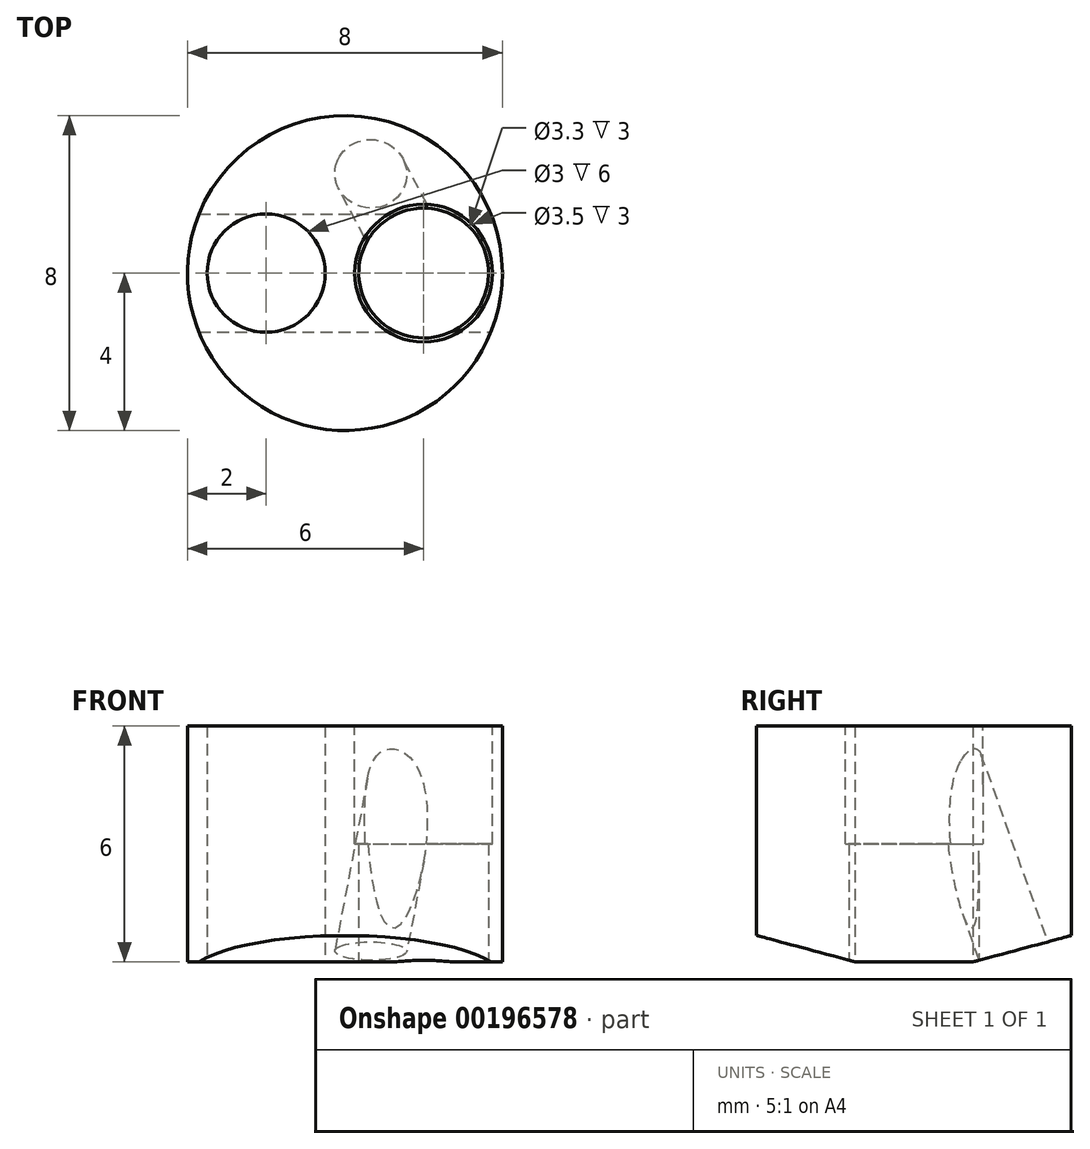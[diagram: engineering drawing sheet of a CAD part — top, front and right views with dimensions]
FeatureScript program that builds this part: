
annotation { "Feature Type Name" : "Feature", "Feature Type Description" : "" }
export const myFeature = defineFeature(function(context is Context, id is Id, definition is map)
    precondition{}
    {
        {
            var Q0;
            Q0=qCreatedBy(makeId("Top.planeOp"),FACE);
            var sketch = newSketch(context, id + "F0", { "sketchPlane" : qUnion([Q0])});
            skCircle(sketch, "E0", {"center": v(0, 0) * mm, "radius": 4 * mm});
            skCircle(sketch, "E1", {"center": v(-2, 0) * mm, "radius": 1.5 * mm});
            skPoint(sketch, "E2", {"position": v(2, 0) * mm});
            skLineSegment(sketch, "E3", {"start": v(0, -7.13) * mm, "end": v(0, 13.24) * mm, "construction": true});
            skSolve(sketch);
        }
        {
            var Q0;
            Q0 = qSketchRegion(id + "F0", true);
            extrude(context, id + "F1", {"entities" : qUnion([Q0]), "depth" : 6 * mm});
        }
        {
            var Q0;
            Q0=sQuery(id+"F0.wireOp",VERTEX,"E2");
            var Q1;
            Q1=makeQuery(id+"F1.opExtrude","SWEPT_BODY",BODY,{"disambiguationData":[OSD([sQuery(id+"F0.wireOp",EDGE,"E0"),sQuery(id+"F0.wireOp",EDGE,"E1")])]});
            hole(context, id + "F2", {"style" : HoleStyle.SIMPLE, "endStyle" : HoleEndStyle.BLIND, "oppositeDirection" : true, "standardTappedOrClearance" : lookupTablePath({ "standard" : "ISO", "fit" : "Normal", "size" : "M3", "type" : "Clearance" }), "standardBlindInLast" : lookupTablePath({ "fit" : "Standard", "standard" : "ISO", "size" : "M3", "type" : "Clearance" }), "holeDiameter" : 3.3 * mm, "holeDepth" : 3 * mm, "locations" : qUnion([Q0]), "scope" : qUnion([Q1])});
        }
        {
            var Q0;
            Q0=qCreatedBy(makeId("Right.planeOp"),FACE);
            var sketch = newSketch(context, id + "F3", { "sketchPlane" : qUnion([Q0])});
            skLineSegment(sketch, "E4", {"start": v(1.5, 0) * mm, "end": v(6.98, 1.47) * mm});
            skLineSegment(sketch, "E5", {"start": v(6.98, 1.47) * mm, "end": v(6.98, 0) * mm});
            skLineSegment(sketch, "E6", {"start": v(6.98, 0) * mm, "end": v(1.5, 0) * mm});
            skLineSegment(sketch, "E7", {"start": v(0, 0) * mm, "end": v(0, 8.53) * mm, "construction": true});
            skLineSegment(sketch, "E8.MirrorCS", {"start": v(-6.98, 1.47) * mm, "end": v(-6.98, 0) * mm});
            skLineSegment(sketch, "E9.MirrorCS", {"start": v(-6.98, 0) * mm, "end": v(-1.5, 0) * mm});
            skLineSegment(sketch, "E10.MirrorCS", {"start": v(-1.5, 0) * mm, "end": v(-6.98, 1.47) * mm});
            skSolve(sketch);
        }
        {
            var Q0;
            Q0 = qSketchRegion(id + "F3", true);
            var Q1;
            Q1=makeQuery(id+"F1.opExtrude","SWEPT_BODY",BODY,{"disambiguationData":[OSD([sQuery(id+"F0.wireOp",EDGE,"E0"),sQuery(id+"F0.wireOp",EDGE,"E1")])]});
            extrude(context, id + "F4", {"entities" : qUnion([Q0]), "operationType" : NewBodyOperationType.REMOVE, "endBound" : BoundingType.THROUGH_ALL, "oppositeDirection" : true, "endBoundEntityBody" : qUnion([Q1]), "depth" : 25 * mm, "hasSecondDirection" : true, "secondDirectionBound" : SecondDirectionBoundingType.THROUGH_ALL, "secondDirectionOppositeDirection" : false, "secondDirectionDepth" : 25 * mm});
        }
        {
            var Q0;
            Q0=makeQuery(id+"F1.opExtrude","CAP_FACE",FACE,{"disambiguationData":[OSD([sQuery(id+"F0.wireOp",EDGE,"E0"),sQuery(id+"F0.wireOp",EDGE,"E1")])],"isStart":false});
            var sketch = newSketch(context, id + "F5", { "sketchPlane" : qUnion([Q0])});
            skPoint(sketch, "E11.0", {"position": v(2, 0) * mm});
            skCircle(sketch, "E12", {"center": v(2, 0) * mm, "radius": 1.75 * mm});
            skSolve(sketch);
        }
        {
            var Q0;
            Q0 = qSketchRegion(id + "F5", true);
            extrude(context, id + "F6", {"entities" : qUnion([Q0]), "operationType" : NewBodyOperationType.REMOVE, "oppositeDirection" : true, "depth" : 3 * mm});
        }
        {
            var Q0;
            Q0=qCreatedBy(makeId("Front.planeOp"),FACE);
            var sketch = newSketch(context, id + "F7", { "sketchPlane" : qUnion([Q0])});
            skLineSegment(sketch, "E13", {"start": v(2, -0.97) * mm, "end": v(2, 7.35) * mm, "construction": true});
            skSolve(sketch);
        }
        {
            var Q0;
            Q0=sQuery(id+"F7.wireOp",EDGE,"E13");
            cPlane(context, id + "F8", {"entities" : qUnion([Q0]), "cplaneType" : CPlaneType.LINE_ANGLE, "offset" : 25 * mm, "angle" : 28 * degree, "width" : 150 * mm, "height" : 150 * mm});
        }
        {
            var Q0;
            Q0=qCreatedBy(id+"F8.planeOp",FACE);
            var sketch = newSketch(context, id + "F9", { "sketchPlane" : qUnion([Q0])});
            skLineSegment(sketch, "E14", {"start": v(-1.52, 8.79) * mm, "end": v(2.17, -0.34) * mm});
            skLineSegment(sketch, "E15", {"start": v(2.17, -0.34) * mm, "end": v(3, 0) * mm});
            skLineSegment(sketch, "E16", {"start": v(3, 0) * mm, "end": v(-2.05, 12.5) * mm});
            skLineSegment(sketch, "E17", {"start": v(-2.05, 12.5) * mm, "end": v(-1.52, 8.79) * mm});
            skSolve(sketch);
        }
        {
            var Q0;
            Q0 = qSketchRegion(id + "F9", true);
            var Q1;
            Q1 = qConstructionFilter(qBodyType(qCreatedBy(id + "F9" ,EDGE), BodyType.WIRE), ConstructionObject.NO);
            var Q2;
            Q2=sQuery(id+"F9.wireOp",EDGE,"E14");
            revolve(context, id + "F10", {"operationType" : NewBodyOperationType.REMOVE, "entities" : qUnion([Q0]), "surfaceEntities" : qUnion([Q1]), "axis" : qUnion([Q2]), "revolveType" : RevolveType.FULL, "oppositeDirection" : true});
        }
    });
